# Revit family: E_Cable Tray Support_MEPcontent_OBO Bettermann_Bracket AWV FT
name_source: partatom
category: Cable Tray Fittings
revit_build: Autodesk Revit MEP 2015 (Build: 20140606_1530(x64)
units: mm (PartAtom-declared; Revit-internal decimal feet)

## types (5) — shared parameters
Article Description = Wall Bracket
Depth = 60 mm  [stored 0.19685 ft]
Description = Wall Bracket
EMCS Version = 2.0
ETIM Article Class = EC000022
Family Version = 10.14
Front Height = 71 mm  [stored 0.23294 ft]
Gray = Color RGB 189-187-185
Height = 130 mm
Height 1 = 130 mm  [stored 0.426509 ft]
IFCExportAs = IfcCableCarrierFittingType
IFCExportType = NOTDEFINED
MEPcontent Class = CABLE_TRAY_SUPPORT
Manufacturer = OBO BETTERMANN
Manufacturer URL = http://catalog4.obo-bettermann.com
Product Line = OBO BETTERMANN CableTrays
Revit Version = 2015
URL = www.stabiplan.com

## per-type parameters (varying)
| type | GTIN | Manufacturer Art. No. | Width | Width 1 |
| AWV 21 FT | 4012196206292 | 6419534 | 210 mm | 210 mm  [stored 0.688976 ft] |
| AWV 31 FT | 4012196206353 | 6419550 | 310 mm | 310 mm  [stored 1.01706 ft] |
| AWV 41 FT | 4012196206414 | 6419577 | 410 mm | 410 mm  [stored 1.34514 ft] |
| AWV 51 FT | 4012196206476 | 6419593 | 510 mm | 510 mm  [stored 1.67323 ft] |
| AWV 61 FT | 4012196206537 | 6419615 | 610 mm | 610 mm  [stored 2.00131 ft] |

note: column(s) folded — value = type name in every type: Article Type, Model

note: [stored X ft] marks values corroborated as IEEE doubles in the binary element streams (Revit-internal decimal feet)

## geometry (parser evidence)
native form markers: Sweep x3
no freeform markers — native parametric forms only
